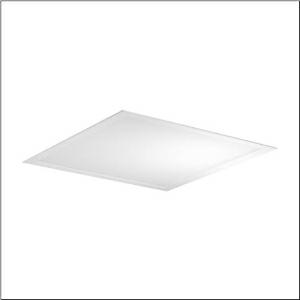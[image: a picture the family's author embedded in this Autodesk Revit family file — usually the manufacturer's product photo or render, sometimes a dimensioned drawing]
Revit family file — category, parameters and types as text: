
# Revit family: apollon_21_square_51mq11w72314
name_source: partatom
category: Lighting Fixtures
units: mm (PartAtom-declared; Revit-internal decimal feet)

## family parameters
Cut with Voids When Loaded = No
Host = Face
Light Source = No
Part Type = Normal
Room Calculation Point = No
Round Connector Dimension = Use Diameter
Shared = No

## types (1)
- Apollon 21 square (1 x LED, 4100 lm, 23.3 W, 3000K)
    Apparent Load = 23 VA
    CIE Flux Codes = 60 87 97 100 100
    Color Rendering = 80
    Color Temperature = 3000K
    Default Elevation = 1800 mm
    Description = Apollon 21 square, office luminaire, primary optical cover: micro prismatic cover, of PMMA, CAT 2 (L<= 3000cd/m²), light emission: direct distribution, primary light characteristic: symmetric, installation type: lay-in mounting, LED, rated luminous flux: 4.100lm, luminous efficacy: 176lm/W, light colour: 830, colour temperature: 3000K, control gear: ON/OFF, with terminal, 3-pole, mains connection: 220..240V, AC/DC, 0/50..60Hz, rated input power: 23.3W, housing, of aluminium, coated, traffic white (RAL 9016), module: M625, length: 620mm, width: 620mm, height: 55mm, recess depth: 180mm, housing upper side, of sheet steel, galvanised, protection rating (complete): IP20, protection rating (lamp compartment, on room side): IP50, insulation class (complete): insulation class II (safety insulation), certification: CE, ENEC, impact resistance: IK03, permissible operating ambient temperature: -20..+45°C, permissible storage temperature: -40..+80°C, standard: EN 60598-2-22, packaging unit: 1 piece
    Height = 0 mm  [stored 0 ft]
    Lamp = 1 x LED
    Lamp Light Flux = 4100 lm
    Lamp Power = 23.3 W
    Lamp count = 1
    Length = 620 mm
    Luminous efficacy = 176 lm/W
    Manufacturer = Siteco
    ModVariant = No
    Model = 51MQ11W72314
    Mounting Place = Ceiling
    Mounting Type = Recessed
    Number of Poles = 1
    OnlyDefault = Yes
    Power Factor = 1
    Product Name = Apollon 21 square
    Product group = office luminaire | ceiling recessed
    ProductGroupID = 401
    Protection Class = Protection class II
    Protection Degree = IP 20
    RLX_Detail_Level = 1
    RLX_Emergency_Light_Flux = 0 lm
    RLX_Emergency_Type = 0
    RLX_Emergency_Type_DB = No
    RlxData = <blob elided: 13021 chars, md5=7c7f3c2b>
    Socket = socket
    Standby Power = 0 W
    System Light Flux = 4100 lm
    System Power = 23 W
    Type Comments = Product without accessories
    Type Image = l_1291054.jpg
    URL = http://relux.com
    VarID = ---
    Voltage = 0 V
    Weight = 0.00 kg
    Width = 620 mm

note: [stored X ft] marks values corroborated as IEEE doubles in the binary element streams (Revit-internal decimal feet)

## geometry (parser evidence)
native form markers: Sweep x10
no freeform markers — native parametric forms only
